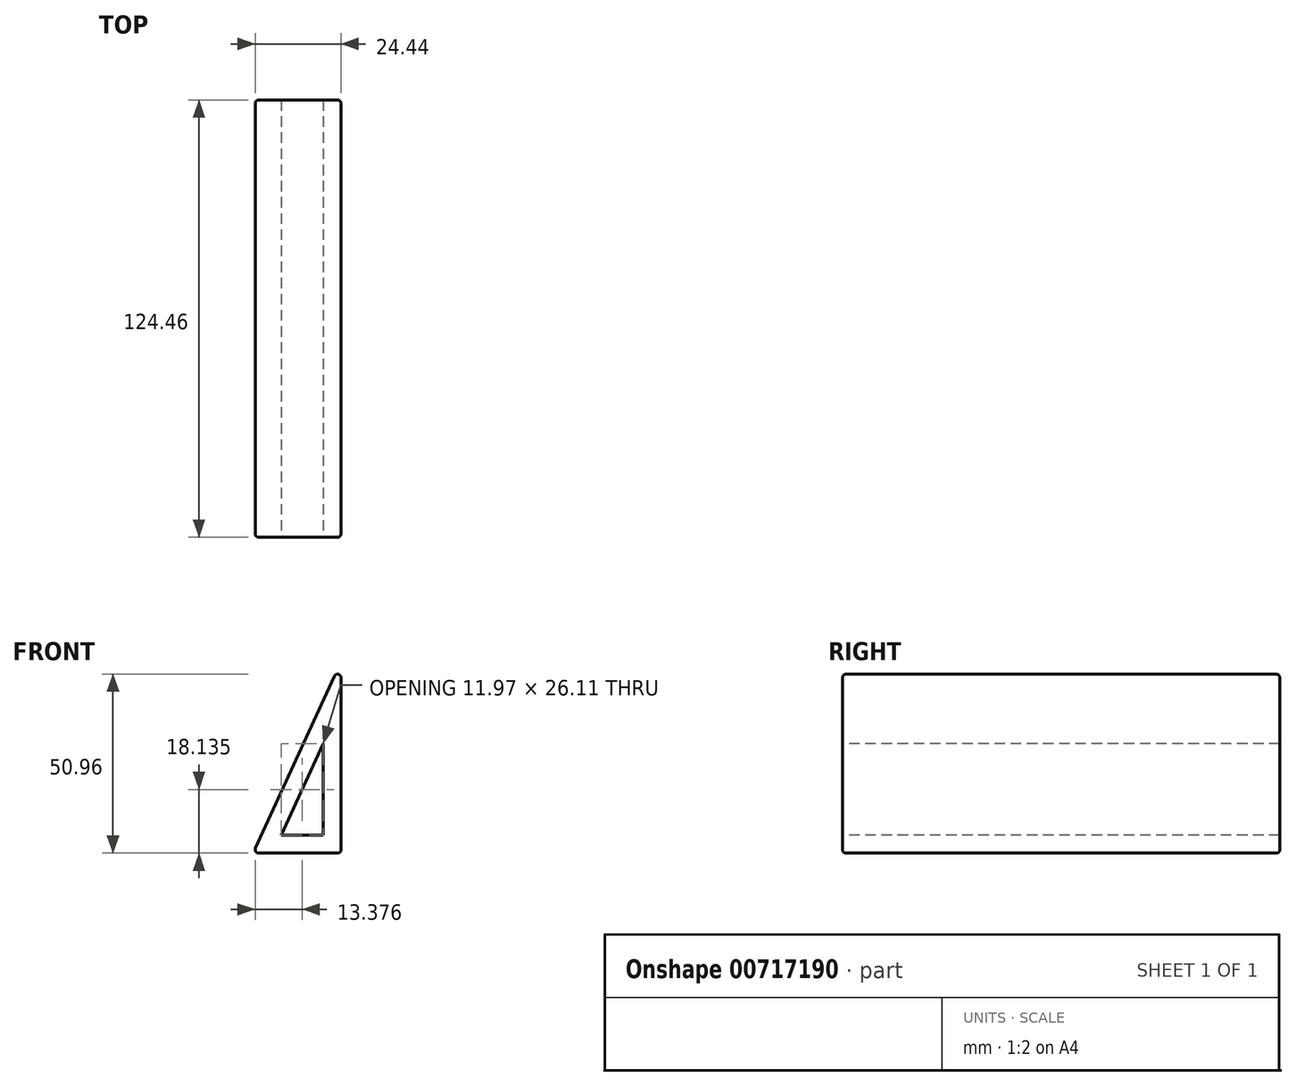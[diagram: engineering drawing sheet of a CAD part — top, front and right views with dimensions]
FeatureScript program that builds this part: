
annotation { "Feature Type Name" : "Feature", "Feature Type Description" : "" }
export const myFeature = defineFeature(function(context is Context, id is Id, definition is map)
    precondition{}
    {
        {
            var Q0;
            Q0=qCreatedBy(makeId("Front.planeOp"),FACE);
            var sketch = newSketch(context, id + "F0", { "sketchPlane" : qUnion([Q0])});
            skLineSegment(sketch, "E0", {"start": v(0, 0) * mm, "end": v(-25, 0) * mm});
            skLineSegment(sketch, "E1", {"start": v(-25, 0) * mm, "end": v(0, 54.54) * mm});
            skLineSegment(sketch, "E2", {"start": v(0, 54.54) * mm, "end": v(0, 0) * mm});
            skSolve(sketch);
        }
        {
            var Q0;
            Q0 = qSketchRegion(id + "F0", true);
            extrude(context, id + "F1", {"entities" : qUnion([Q0]), "depth" : 124.46 * mm, "offsetDistance" : 25.4 * mm});
        }
        {
            var Q0;
            Q0=makeQuery(id+"F1.opExtrude","CAP_FACE",FACE,{"disambiguationData":[OSD([sQuery(id+"F0.wireOp",EDGE,"E0"),sQuery(id+"F0.wireOp",EDGE,"E1"),sQuery(id+"F0.wireOp",EDGE,"E2")])],"isStart":false});
            var sketch = newSketch(context, id + "F2", { "sketchPlane" : qUnion([Q0])});
            skLineSegment(sketch, "E3", {"start": v(-17.05, 5.08) * mm, "end": v(-5.08, 31.19) * mm});
            skLineSegment(sketch, "E4", {"start": v(-5.08, 31.19) * mm, "end": v(-5.08, 5.08) * mm});
            skLineSegment(sketch, "E5", {"start": v(-5.08, 5.08) * mm, "end": v(-17.05, 5.08) * mm});
            skSolve(sketch);
        }
        {
            var Q0;
            Q0 = qSketchRegion(id + "F2", true);
            var Q1;
            Q1=makeQuery(id+"F1.opExtrude","CAP_FACE",FACE,{"disambiguationData":[OSD([sQuery(id+"F0.wireOp",EDGE,"E0"),sQuery(id+"F0.wireOp",EDGE,"E1"),sQuery(id+"F0.wireOp",EDGE,"E2")])],"isStart":true});
            extrude(context, id + "F3", {"entities" : qUnion([Q0]), "operationType" : NewBodyOperationType.REMOVE, "endBound" : BoundingType.UP_TO_SURFACE, "oppositeDirection" : true, "depth" : 147.83 * mm, "endBoundEntityFace" : qUnion([Q1]), "offsetDistance" : 25.4 * mm});
        }
        {
            var Q0;
            Q0=makeQuery(id+"F1.opExtrude","SWEPT_EDGE",EDGE,{"disambiguationData":[OSD([sQuery(id+"F0.wireOp",EDGE,"E1"),sQuery(id+"F0.wireOp",EDGE,"E2")])]});
            var Q1;
            Q1=makeQuery(id+"F1.opExtrude","CAP_EDGE",EDGE,{"disambiguationData":[OSD([sQuery(id+"F0.wireOp",EDGE,"E1")])],"isStart":true});
            var Q2;
            Q2=makeQuery(id+"F1.opExtrude","SWEPT_EDGE",EDGE,{"disambiguationData":[OSD([sQuery(id+"F0.wireOp",EDGE,"E0"),sQuery(id+"F0.wireOp",EDGE,"E1")])]});
            var Q3;
            Q3=makeQuery(id+"F1.opExtrude","CAP_EDGE",EDGE,{"disambiguationData":[OSD([sQuery(id+"F0.wireOp",EDGE,"E1")])],"isStart":false});
            var Q4;
            Q4=makeQuery(id+"F1.opExtrude","CAP_EDGE",EDGE,{"disambiguationData":[OSD([sQuery(id+"F0.wireOp",EDGE,"E0")])],"isStart":false});
            var Q5;
            Q5=makeQuery(id+"F1.opExtrude","CAP_EDGE",EDGE,{"disambiguationData":[OSD([sQuery(id+"F0.wireOp",EDGE,"E2")])],"isStart":false});
            var Q6;
            Q6=makeQuery(id+"F3.boolean.opBoolean","COPY",EDGE,{"derivedFrom":makeQuery(id+"F3.opExtrude","CAP_EDGE",EDGE,{"disambiguationData":[OSD([sQuery(id+"F2.wireOp",EDGE,"E5")])],"isStart":true})});
            var Q7;
            Q7=makeQuery(id+"F3.boolean.opBoolean","COPY",EDGE,{"derivedFrom":makeQuery(id+"F3.opExtrude","CAP_EDGE",EDGE,{"disambiguationData":[OSD([sQuery(id+"F2.wireOp",EDGE,"E3")])],"isStart":true})});
            var Q8;
            Q8=makeQuery(id+"F3.boolean.opBoolean","COPY",EDGE,{"derivedFrom":makeQuery(id+"F3.opExtrude","CAP_EDGE",EDGE,{"disambiguationData":[OSD([sQuery(id+"F2.wireOp",EDGE,"E4")])],"isStart":true})});
            var Q9;
            Q9=makeQuery(id+"F1.opExtrude","CAP_EDGE",EDGE,{"disambiguationData":[OSD([sQuery(id+"F0.wireOp",EDGE,"E0")])],"isStart":true});
            var Q10;
            Q10=makeQuery(id+"F1.opExtrude","SWEPT_EDGE",EDGE,{"disambiguationData":[OSD([sQuery(id+"F0.wireOp",EDGE,"E0"),sQuery(id+"F0.wireOp",EDGE,"E2")])]});
            var Q11;
            Q11=makeQuery(id+"F3.boolean.opBoolean","COPY",EDGE,{"derivedFrom":makeQuery(id+"F3.opExtrude","CAP_EDGE",EDGE,{"disambiguationData":[OSD([sQuery(id+"F2.wireOp",EDGE,"E4")])],"isStart":false})});
            var Q12;
            Q12=makeQuery(id+"F3.boolean.opBoolean","COPY",EDGE,{"derivedFrom":makeQuery(id+"F3.opExtrude","CAP_EDGE",EDGE,{"disambiguationData":[OSD([sQuery(id+"F2.wireOp",EDGE,"E5")])],"isStart":false})});
            var Q13;
            Q13=makeQuery(id+"F3.boolean.opBoolean","COPY",EDGE,{"derivedFrom":makeQuery(id+"F3.opExtrude","CAP_EDGE",EDGE,{"disambiguationData":[OSD([sQuery(id+"F2.wireOp",EDGE,"E3")])],"isStart":false})});
            var Q14;
            Q14=makeQuery(id+"F1.opExtrude","CAP_EDGE",EDGE,{"disambiguationData":[OSD([sQuery(id+"F0.wireOp",EDGE,"E2")])],"isStart":true});
            fillet(context, id + "F4", {"entities" : qUnion([Q0, Q1, Q2, Q3, Q4, Q5, Q6, Q7, Q8, Q9, Q10, Q11, Q12, Q13, Q14]), "radius" : 1 * mm, "tangentPropagation" : true, "allowEdgeOverflow" : false});
        }
    });
